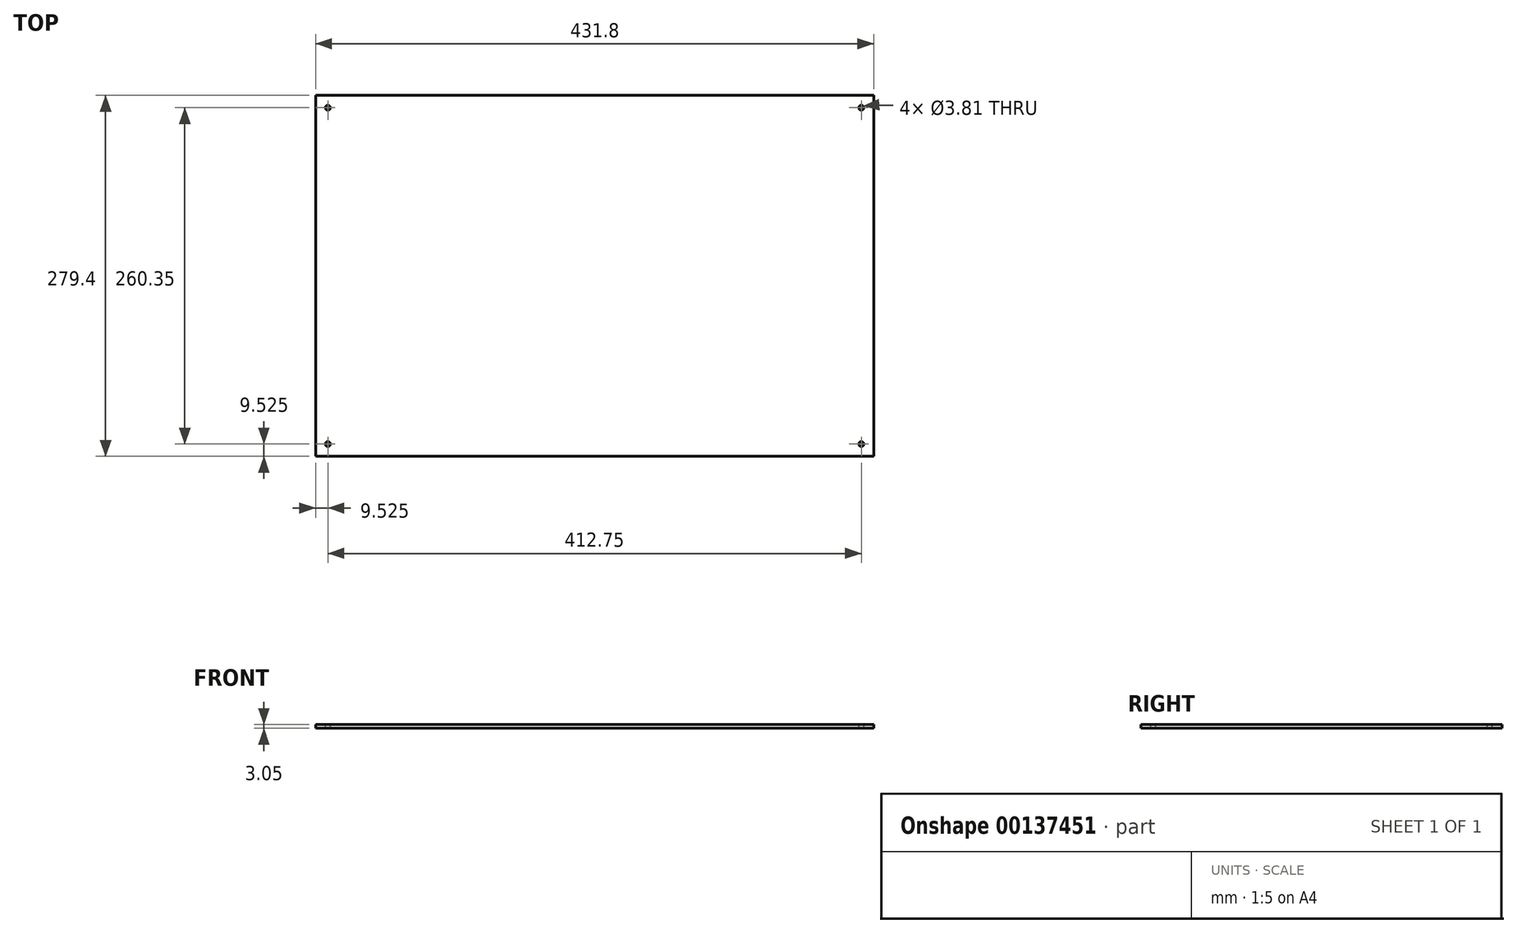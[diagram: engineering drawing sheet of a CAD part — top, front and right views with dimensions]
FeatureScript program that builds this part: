
annotation { "Feature Type Name" : "Feature", "Feature Type Description" : "" }
export const myFeature = defineFeature(function(context is Context, id is Id, definition is map)
    precondition{}
    {
        {
            var Q0;
            Q0=qCreatedBy(makeId("Top.planeOp"),FACE);
            var sketch = newSketch(context, id + "F0", { "sketchPlane" : qUnion([Q0])});
            skLineSegment(sketch, "E0.bottom", {"start": v(-215.9, 139.7) * mm, "end": v(215.9, 139.7) * mm});
            skLineSegment(sketch, "E0.top", {"start": v(-215.9, -139.7) * mm, "end": v(215.9, -139.7) * mm});
            skLineSegment(sketch, "E0.left", {"start": v(-215.9, 139.7) * mm, "end": v(-215.9, -139.7) * mm});
            skLineSegment(sketch, "E0.right", {"start": v(215.9, 139.7) * mm, "end": v(215.9, -139.7) * mm});
            skSolve(sketch);
        }
        {
            var Q0;
            Q0 = qSketchRegion(id + "F0", true);
            extrude(context, id + "F1", {"entities" : qUnion([Q0]), "depth" : 3.05 * mm});
        }
        {
            var Q0;
            Q0=makeQuery(id+"F1.opExtrude","CAP_FACE",FACE,{"disambiguationData":[OSD([sQuery(id+"F0.wireOp",EDGE,"E0.bottom"),sQuery(id+"F0.wireOp",EDGE,"E0.top"),sQuery(id+"F0.wireOp",EDGE,"E0.left"),sQuery(id+"F0.wireOp",EDGE,"E0.right")])],"isStart":false});
            var sketch = newSketch(context, id + "F2", { "sketchPlane" : qUnion([Q0])});
            skCircle(sketch, "E1", {"center": v(-206.37, 130.18) * mm, "radius": 1.9 * mm});
            skCircle(sketch, "E2.MirrorC", {"center": v(206.37, 130.18) * mm, "radius": 1.9 * mm});
            skCircle(sketch, "E3.MirrorC", {"center": v(-206.37, -130.18) * mm, "radius": 1.9 * mm});
            skCircle(sketch, "E4.MirrorC", {"center": v(206.37, -130.18) * mm, "radius": 1.9 * mm});
            skSolve(sketch);
        }
        {
            var Q0;
            Q0 = qSketchRegion(id + "F2", true);
            extrude(context, id + "F3", {"entities" : qUnion([Q0]), "operationType" : NewBodyOperationType.REMOVE, "endBound" : BoundingType.THROUGH_ALL, "oppositeDirection" : true, "depth" : 25.4 * mm});
        }
    });
